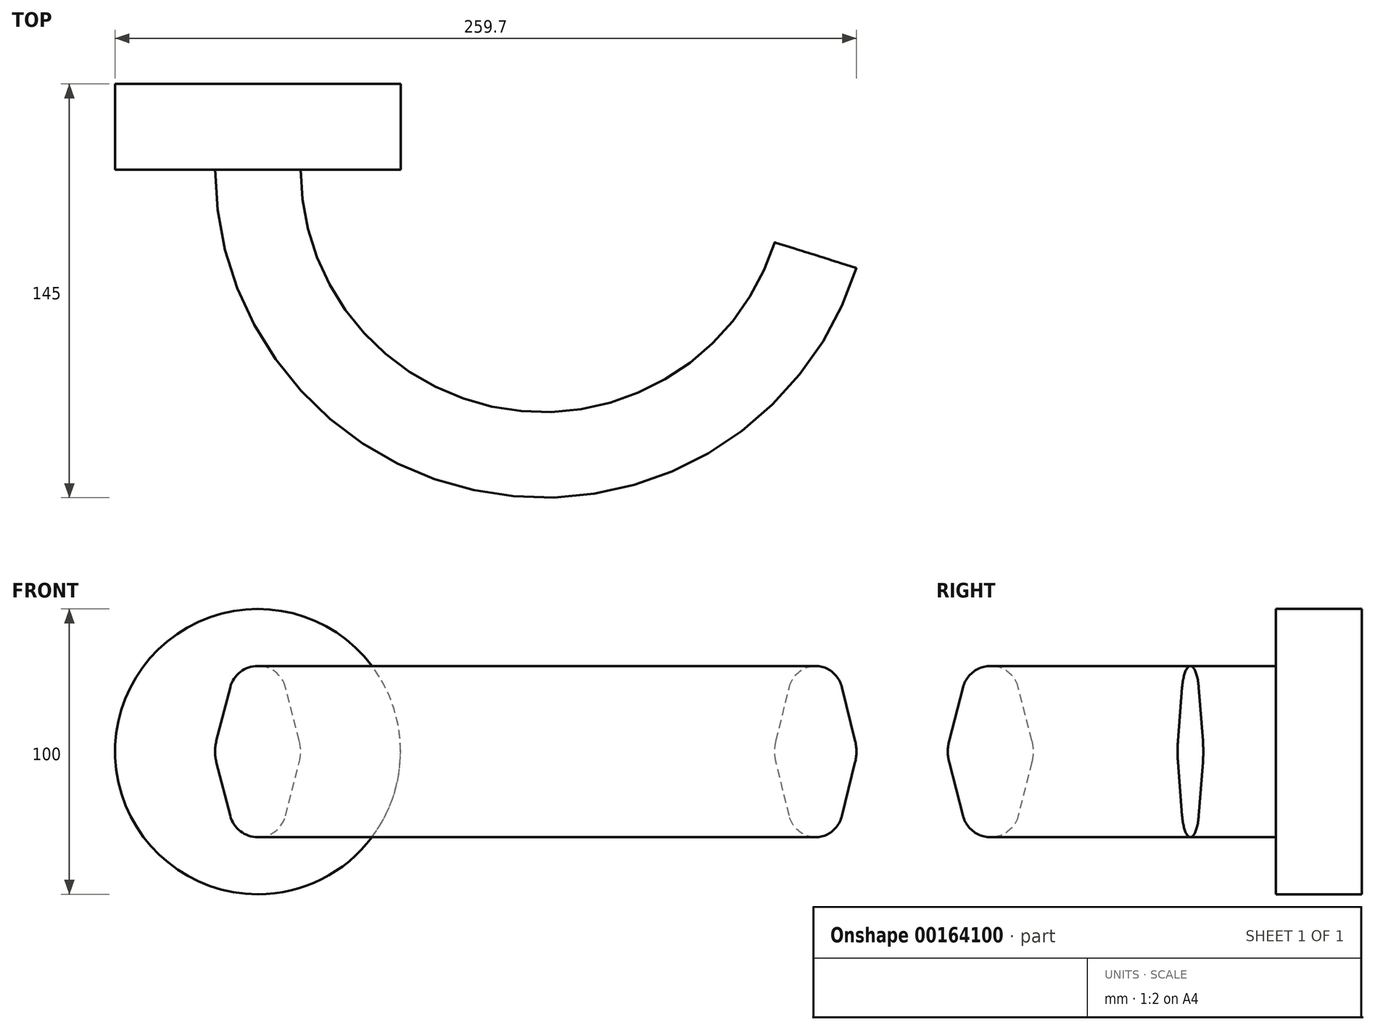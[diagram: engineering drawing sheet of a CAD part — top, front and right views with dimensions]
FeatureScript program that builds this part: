
annotation { "Feature Type Name" : "Feature", "Feature Type Description" : "" }
export const myFeature = defineFeature(function(context is Context, id is Id, definition is map)
    precondition{}
    {
        {
            var Q0;
            Q0=qCreatedBy(makeId("Front.planeOp"),FACE);
            var sketch = newSketch(context, id + "F0", { "sketchPlane" : qUnion([Q0])});
            skCircle(sketch, "E0", {"center": v(0, 0) * mm, "radius": 50 * mm});
            skSolve(sketch);
        }
        {
            var Q0;
            Q0 = qSketchRegion(id + "F0", true);
            extrude(context, id + "F1", {"entities" : qUnion([Q0]), "depth" : 30 * mm});
        }
        {
            var Q0;
            Q0=qCreatedBy(makeId("Top.planeOp"),FACE);
            var sketch = newSketch(context, id + "F2", { "sketchPlane" : qUnion([Q0])});
            skArc(sketch, "E1", {"start": v(0, -30) * mm, "mid": v(84.82, -128.84) * mm, "end": v(195.4, -60) * mm});
            skSolve(sketch);
        }
        {
            var Q0;
            Q0=sQuery(id+"F2.wireOp",VERTEX,"E1.end");
            var Q1;
            Q1=sQuery(id+"F2.wireOp",EDGE,"E1");
            cPlane(context, id + "F3", {"entities" : qUnion([Q0, Q1]), "cplaneType" : CPlaneType.CURVE_POINT, "offset" : 25 * mm, "width" : 150 * mm, "height" : 150 * mm});
        }
        {
            var Q0;
            Q0=qCreatedBy(id+"F3.planeOp",FACE);
            var sketch = newSketch(context, id + "F4", { "sketchPlane" : qUnion([Q0])});
            skArc(sketch, "E2", {"start": v(-189.87, -3.75) * mm, "mid": v(-189.4, 0) * mm, "end": v(-189.87, 3.75) * mm});
            skArc(sketch, "E3", {"start": v(-194.71, 22.5) * mm, "mid": v(-204.4, 30) * mm, "end": v(-214.08, 22.5) * mm});
            skLineSegment(sketch, "E4", {"start": v(-146.02, 0) * mm, "end": v(-255.37, 0) * mm, "construction": true});
            skArc(sketch, "E5.MirrorC", {"start": v(-194.71, -22.5) * mm, "mid": v(-204.4, -30) * mm, "end": v(-214.08, -22.5) * mm});
            skLineSegment(sketch, "E6", {"start": v(-214.08, -22.5) * mm, "end": v(-218.92, -3.75) * mm});
            skLineSegment(sketch, "E7", {"start": v(-194.71, -22.5) * mm, "end": v(-189.87, -3.75) * mm});
            skLineSegment(sketch, "E8.trimOffspring", {"start": v(-218.92, 3.75) * mm, "end": v(-214.08, 22.5) * mm});
            skLineSegment(sketch, "E9.trimOffspring", {"start": v(-189.87, 3.75) * mm, "end": v(-194.71, 22.5) * mm});
            skArc(sketch, "E10.trimOffspring", {"start": v(-218.92, 3.75) * mm, "mid": v(-219.4, 0) * mm, "end": v(-218.92, -3.75) * mm});
            skSolve(sketch);
        }
        {
            var Q0;
            Q0 = qSketchRegion(id + "F4", true);
            var Q1;
            Q1=sQuery(id+"F2.wireOp",EDGE,"E1");
            sweep(context, id + "F5", {"operationType" : NewBodyOperationType.ADD, "profiles" : qUnion([Q0]), "path" : qUnion([Q1])});
        }
    });
